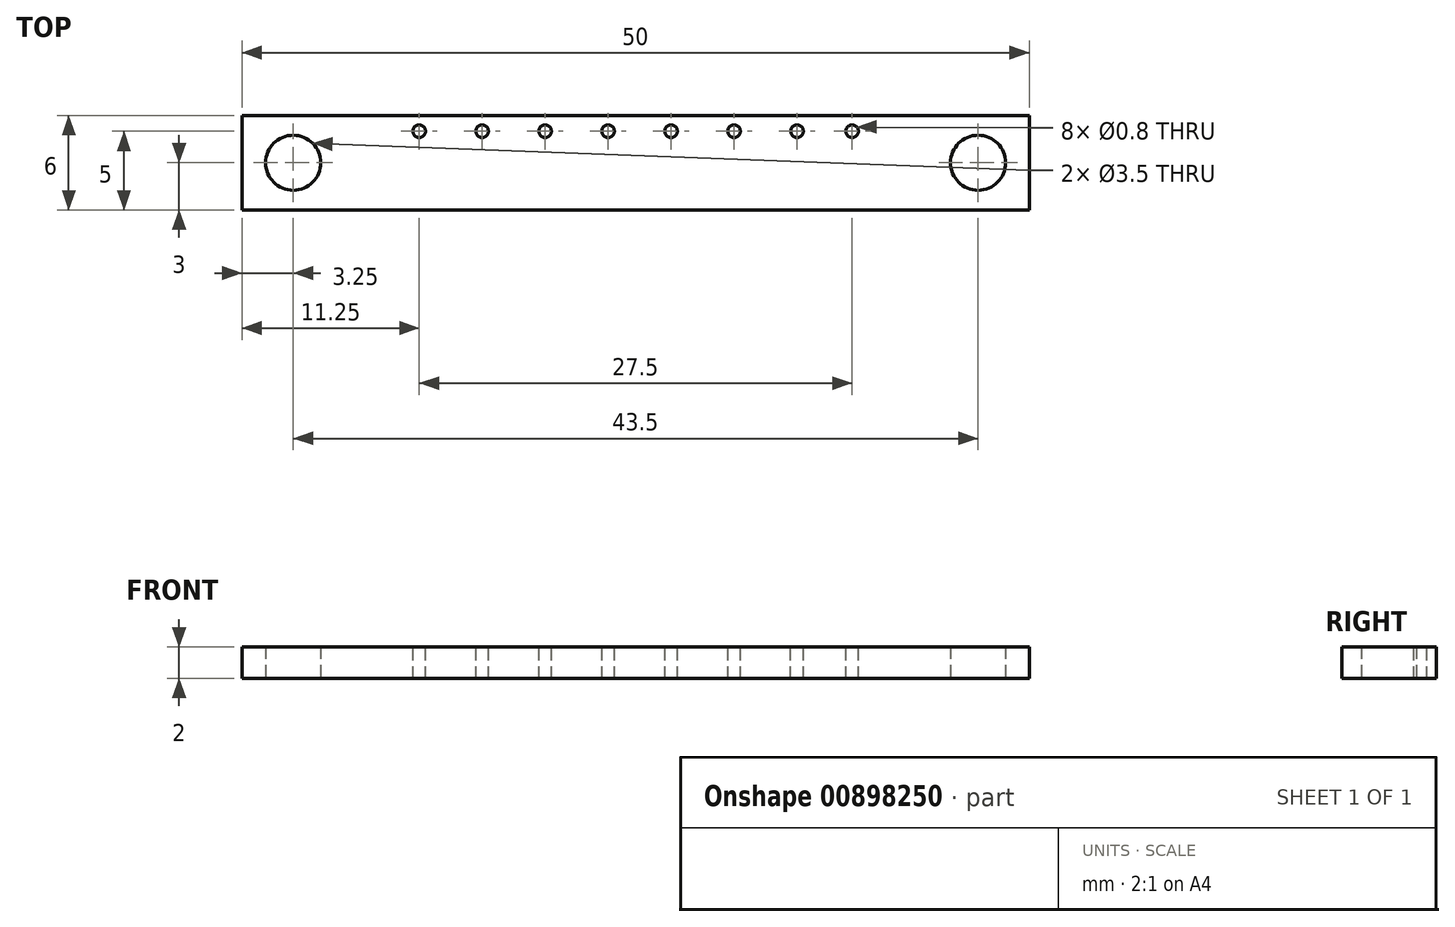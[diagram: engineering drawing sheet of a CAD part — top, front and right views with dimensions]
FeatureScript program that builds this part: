
annotation { "Feature Type Name" : "Feature", "Feature Type Description" : "" }
export const myFeature = defineFeature(function(context is Context, id is Id, definition is map)
    precondition{}
    {
        {
            var Q0;
            Q0=qCreatedBy(makeId("Top.planeOp"),FACE);
            var sketch = newSketch(context, id + "F0", { "sketchPlane" : qUnion([Q0])});
            skLineSegment(sketch, "E0.bottom", {"start": v(0, 0) * mm, "end": v(50, 0) * mm});
            skLineSegment(sketch, "E0.top", {"start": v(0, 6) * mm, "end": v(50, 6) * mm});
            skLineSegment(sketch, "E0.left", {"start": v(0, 0) * mm, "end": v(0, 6) * mm});
            skLineSegment(sketch, "E0.right", {"start": v(50, 0) * mm, "end": v(50, 6) * mm});
            skCircle(sketch, "E1", {"center": v(3.25, 3) * mm, "radius": 1.75 * mm});
            skCircle(sketch, "E2", {"center": v(46.75, 3) * mm, "radius": 1.75 * mm});
            skSolve(sketch);
        }
        {
            var Q0;
            Q0=qSketchRegion(id+"F0",true);
            extrude(context, id + "F1", {"entities" : qUnion([Q0]), "depth" : 2 * mm, "offsetDistance" : 25 * mm});
        }
        {
            var Q0;
            Q0=makeQuery(id+"F1.opExtrude","CAP_FACE",FACE,{"disambiguationData":[OSD([sQuery(id+"F0.wireOp",EDGE,"E0.bottom"),sQuery(id+"F0.wireOp",EDGE,"E0.top"),sQuery(id+"F0.wireOp",EDGE,"E0.left"),sQuery(id+"F0.wireOp",EDGE,"E0.right"),sQuery(id+"F0.wireOp",EDGE,"E1"),sQuery(id+"F0.wireOp",EDGE,"E2")])],"isStart":false});
            var sketch = newSketch(context, id + "F2", { "sketchPlane" : qUnion([Q0])});
            skCircle(sketch, "E3", {"center": v(11.25, 5) * mm, "radius": 0.4 * mm});
            skCircle(sketch, "E4.1.0.0", {"center": v(15.25, 5) * mm, "radius": 0.4 * mm});
            skCircle(sketch, "E4.2.0.0", {"center": v(19.25, 5) * mm, "radius": 0.4 * mm});
            skCircle(sketch, "E4.3.0.0", {"center": v(23.25, 5) * mm, "radius": 0.4 * mm});
            skCircle(sketch, "E4.4.0.0", {"center": v(27.25, 5) * mm, "radius": 0.4 * mm});
            skCircle(sketch, "E4.5.0.0", {"center": v(31.25, 5) * mm, "radius": 0.4 * mm});
            skCircle(sketch, "E4.6.0.0", {"center": v(35.25, 5) * mm, "radius": 0.4 * mm});
            skLineSegment(sketch, "E4.direction1", {"start": v(11.25, 5) * mm, "end": v(15.25, 5) * mm, "construction": true});
            skCircle(sketch, "E5", {"center": v(38.75, 5) * mm, "radius": 0.4 * mm});
            skSolve(sketch);
        }
        {
            var Q0;
            Q0=qSketchRegion(id+"F2",true);
            extrude(context, id + "F3", {"entities" : qUnion([Q0]), "operationType" : NewBodyOperationType.REMOVE, "endBound" : BoundingType.THROUGH_ALL, "oppositeDirection" : true, "depth" : 25 * mm, "offsetDistance" : 25 * mm});
        }
    });
